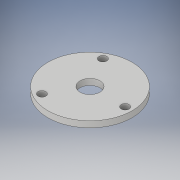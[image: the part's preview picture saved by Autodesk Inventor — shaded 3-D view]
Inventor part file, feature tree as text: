
AUTODESK INVENTOR PART (.ipt)
format: ipt  version: 2019.4 (Build 234330000, 330)  size: 141,312 bytes
history: native  units: in
note: dims shown in document units (in); Inventor stores cm internally (conversion verified against a paired STEP export)
features: other x2, sheet_metal_op x1, sketch x1
ambient origin geometry x8: Origin, YZ Plane, XZ Plane, XY Plane, X Axis, Y Axis, Z Axis, Center Point
bodies: Solid1 (feature_tree)
feature tree (4):
  sheet_metal_op  "Face1"
  sketch  "Sketch1"  dims[d0=1.65in d1=0.3906in d2=0.156in d3=1.1811in d5=360.0deg d7=0.12in]
  other  "Plate1"
  other  "Definition1"
